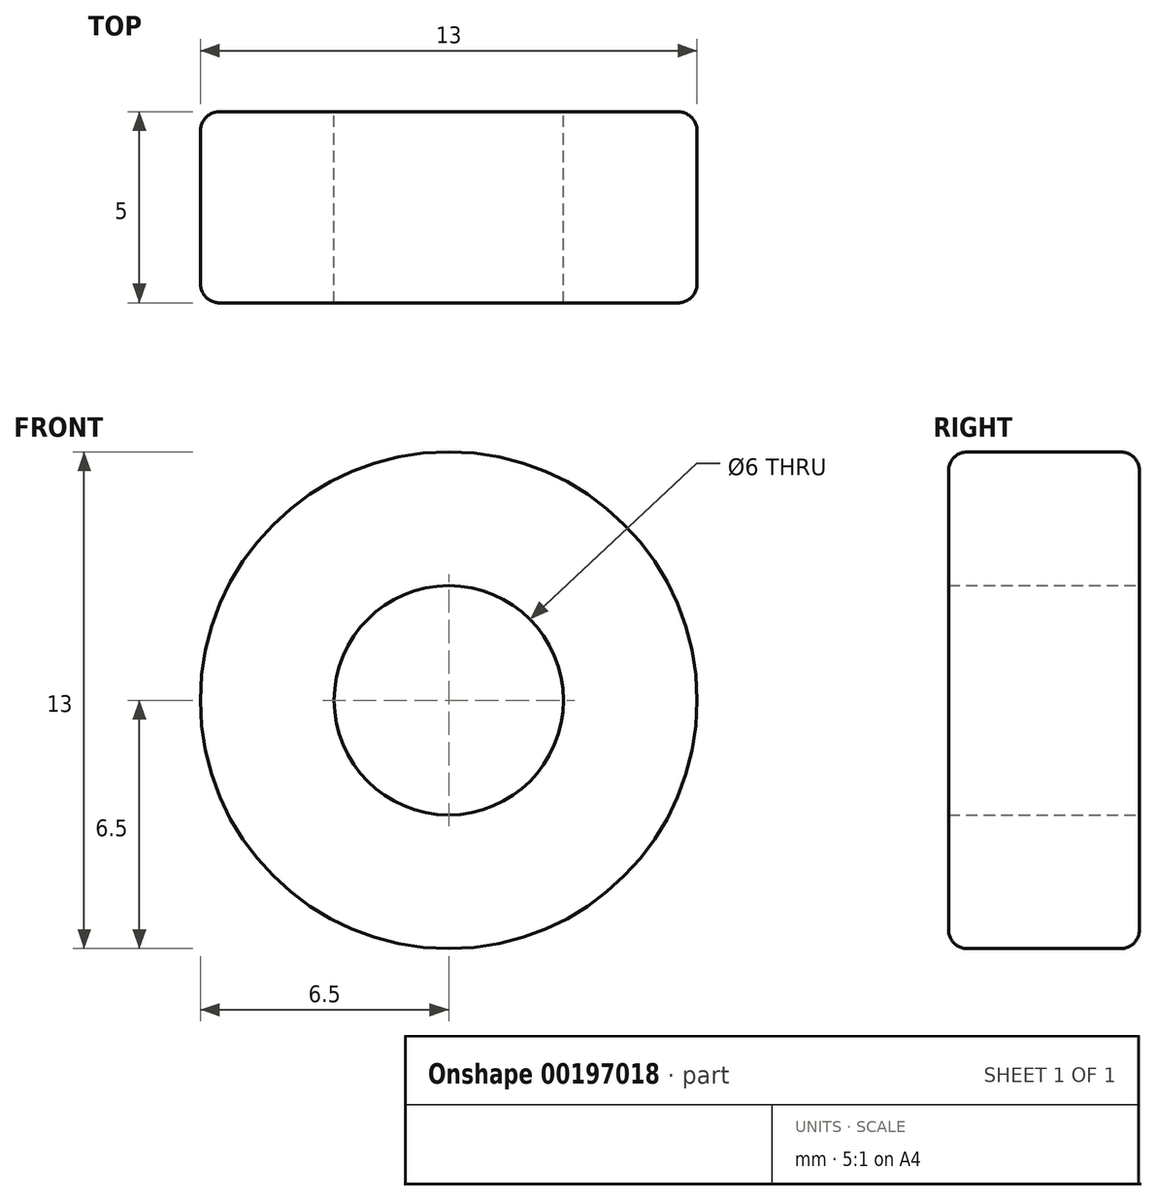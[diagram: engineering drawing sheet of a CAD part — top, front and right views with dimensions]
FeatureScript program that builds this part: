
annotation { "Feature Type Name" : "Feature", "Feature Type Description" : "" }
export const myFeature = defineFeature(function(context is Context, id is Id, definition is map)
    precondition{}
    {
        {
            var Q0;
            Q0=qCreatedBy(makeId("Front.planeOp"),FACE);
            var sketch = newSketch(context, id + "F0", { "sketchPlane" : qUnion([Q0])});
            skCircle(sketch, "E0", {"center": v(0, 0) * mm, "radius": 6.5 * mm});
            skCircle(sketch, "E1", {"center": v(0, 0) * mm, "radius": 3 * mm});
            skSolve(sketch);
        }
        {
            var Q0;
            Q0=makeQuery(id+"F0.imprint","IMPRINT",FACE,{"disambiguationData":[TD([[makeQuery(id+"F0.imprint","IMPRINT",EDGE,{"derivedFrom":sQuery(id+"F0.wireOp",EDGE,"E0")}),1.0]])]});
            extrude(context, id + "F1", {"entities" : qUnion([Q0]), "endBound" : BoundingType.SYMMETRIC, "depth" : 5 * mm});
        }
        {
            var Q0;
            Q0=makeQuery(id+"F1.opExtrude","SWEPT_FACE",FACE,{"disambiguationData":[OSD([sQuery(id+"F0.wireOp",EDGE,"E0")])]});
            fillet(context, id + "F2", {"entities" : qUnion([Q0]), "radius" : .5 * mm, "tangentPropagation" : true, "allowEdgeOverflow" : false});
        }
    });
